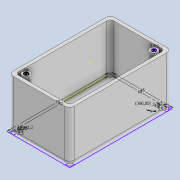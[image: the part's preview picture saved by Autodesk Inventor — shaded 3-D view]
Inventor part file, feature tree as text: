
AUTODESK INVENTOR PART (.ipt)
format: ipt  version: 2020 (Build 240168000, 168)  size: 235,520 bytes
history: native  units: mm
features: extrude x7, sketch x3, fillet x1
ambient origin geometry x8: Origin, YZ Plane, XZ Plane, XY Plane, X Axis, Y Axis, Z Axis, Center Point
bodies: Body1 (feature_tree)
feature tree (11):
  sketch  "Sketch1"  dims[d0=45.0mm d1=75.0mm]
  extrude  "Extrusion3"  Depth=75.0mm
  extrude  "Extrusion4"  Depth=70.0mm
  fillet  "Fillet1"  Radius=2.5mm
  sketch  "Sketch2"  dims[d2=40.0mm d3=70.0mm d8=2.5mm]
  extrude  "Extrusion5"  Depth=2.5mm TaperAngle=0.0deg
  extrude  "Extrusion6"  Depth=37.5mm TaperAngle=0.0deg
  sketch  "Sketch3"  dims[d9=2.5mm d24=2.5mm d25=0.0mm d26=37.5mm d27=0.0mm d28=3.0mm d29=1.5mm d30=1.5mm d31=2.75mm d32=5.5mm d33=1.5mm d34=1.5mm d35=2.75mm d36=45.0deg d37=5.5mm d38=20.0mm d40=360.0deg d43=20.0mm d44=1.2mm d45=1.2mm d46=35.0mm d47=0.0mm d48=10.0mm d49=0.0mm d50=3.0mm d51=2.5mm d52=3.0mm d53=2.5mm d54=0.5mm d55=0.0mm d56=20.0mm d57=0.0mm d58=32.0mm d59=0.0mm d60=0.5mm d61=0.872665mm]
  extrude  "Extrusion7"  Depth=3.0mm
  extrude  "Extrusion8"  Depth=1.5mm
  extrude  "Extrusion9"  Depth=1.5mm
